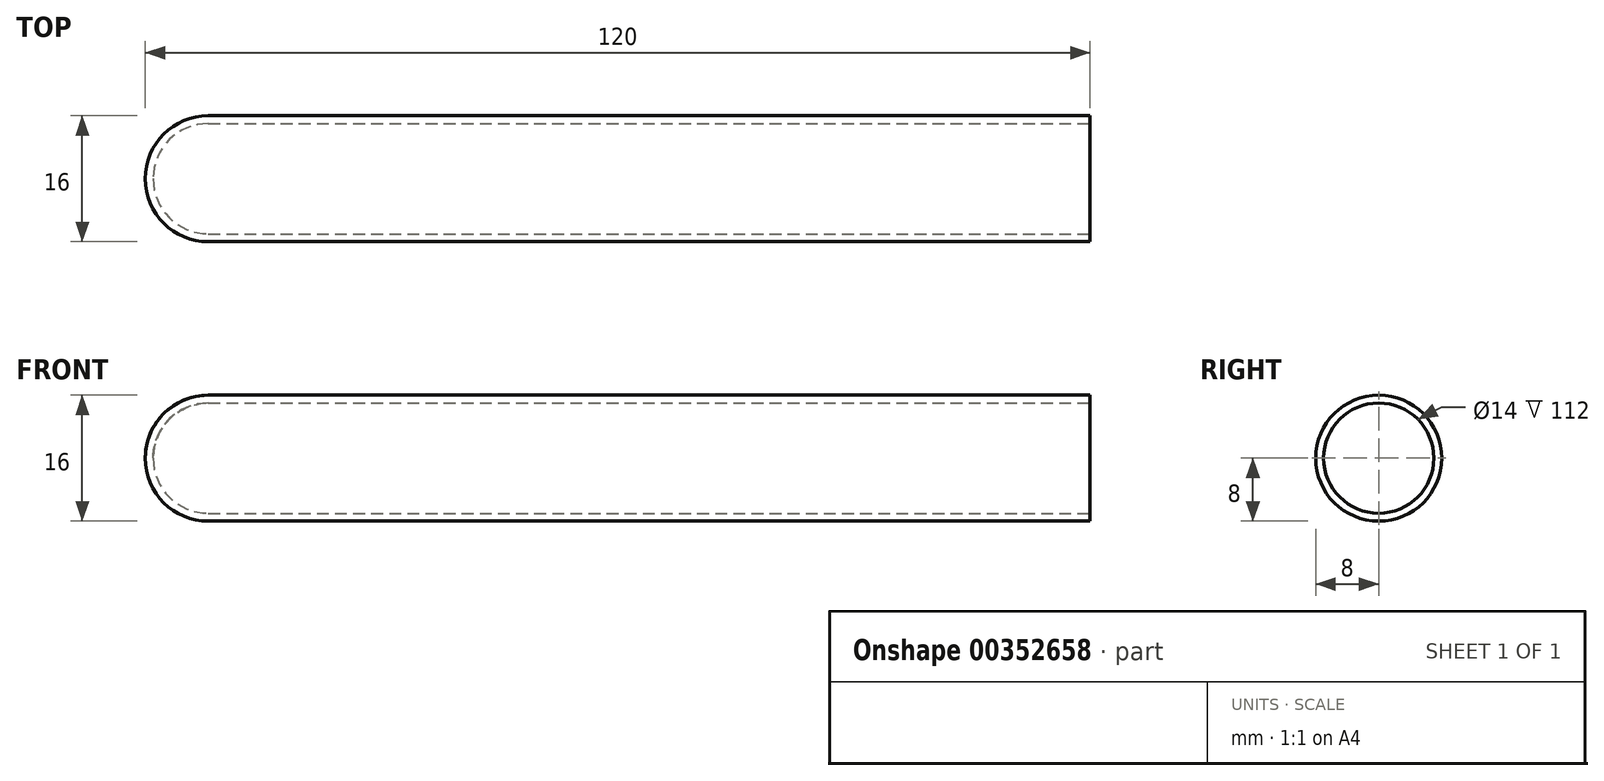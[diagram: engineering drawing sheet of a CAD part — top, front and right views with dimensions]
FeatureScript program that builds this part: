
annotation { "Feature Type Name" : "Feature", "Feature Type Description" : "" }
export const myFeature = defineFeature(function(context is Context, id is Id, definition is map)
    precondition{}
    {
        {
            var Q0;
            Q0=qCreatedBy(makeId("Front.planeOp"),FACE);
            var sketch = newSketch(context, id + "F0", { "sketchPlane" : qUnion([Q0])});
            skArc(sketch, "E0", {"start": v(-112, 8) * mm, "mid": v(-117.66, 5.66) * mm, "end": v(-120, 0) * mm});
            skLineSegment(sketch, "E1", {"start": v(-112, 8) * mm, "end": v(0, 8) * mm});
            skLineSegment(sketch, "E2", {"start": v(0, 8) * mm, "end": v(0, 7) * mm});
            skLineSegment(sketch, "E3", {"start": v(0.07, 0) * mm, "end": v(-120, 0) * mm, "construction": true});
            skArc(sketch, "E4.0", {"start": v(-112, 7) * mm, "mid": v(-116.95, 4.95) * mm, "end": v(-119, 0) * mm});
            skLineSegment(sketch, "E4.1", {"start": v(-112, 7) * mm, "end": v(0, 7) * mm});
            skLineSegment(sketch, "E5", {"start": v(-120, 0) * mm, "end": v(-119, 0) * mm});
            skSolve(sketch);
        }
        {
            var Q0;
            Q0 = qSketchRegion(id + "F0", true);
            var Q1;
            Q1=sQuery(id+"F0.wireOp",EDGE,"E3");
            revolve(context, id + "F1", {"entities" : qUnion([Q0]), "axis" : qUnion([Q1]), "revolveType" : RevolveType.FULL});
        }
    });
